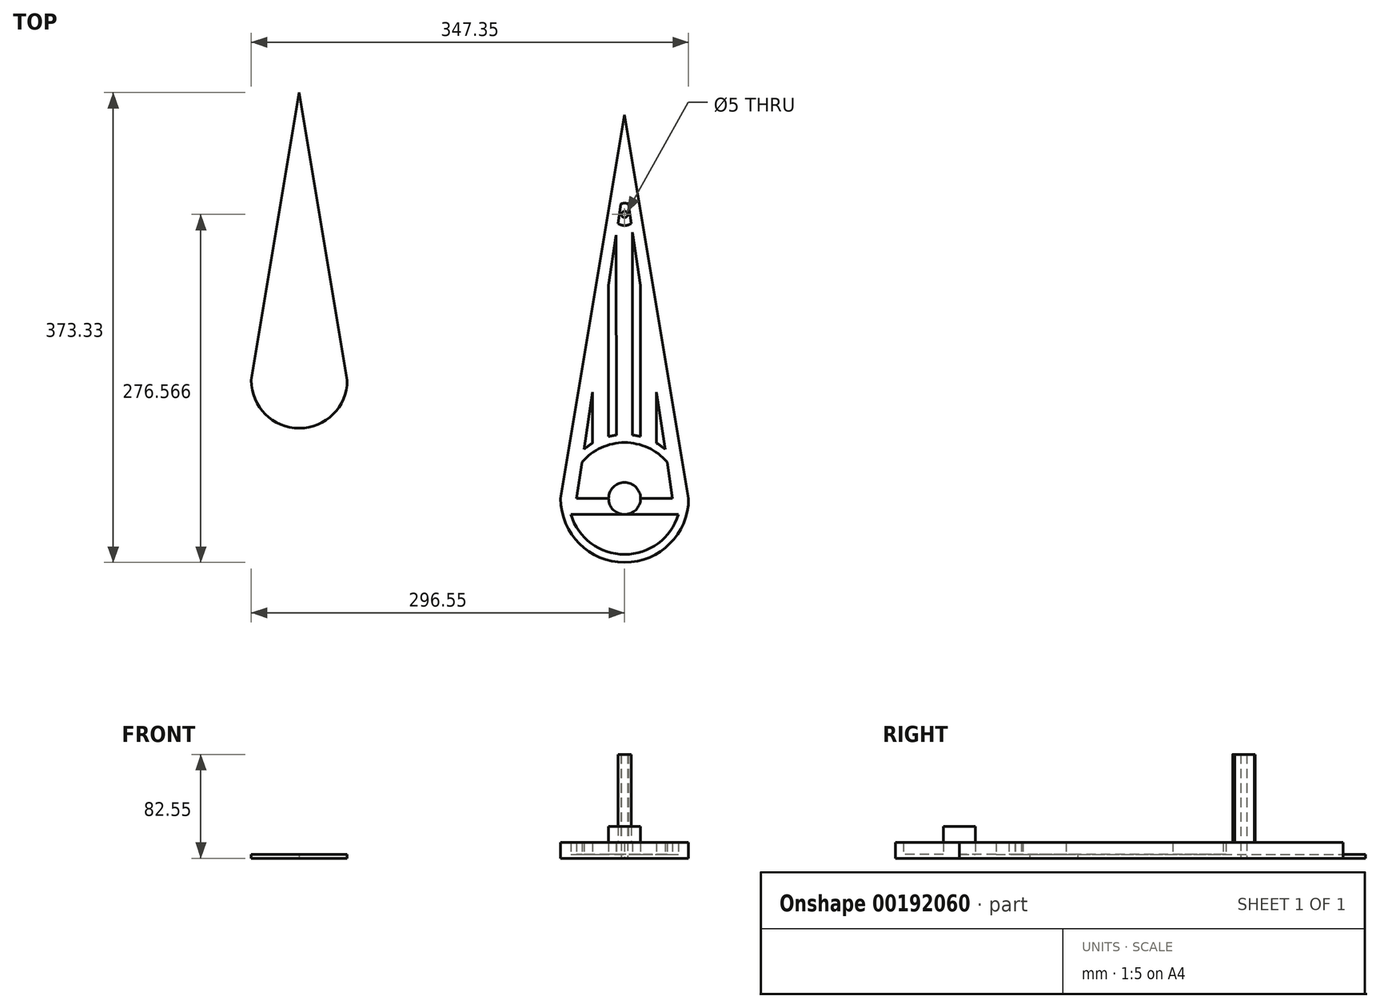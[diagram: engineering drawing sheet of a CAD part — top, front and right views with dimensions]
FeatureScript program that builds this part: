
annotation { "Feature Type Name" : "Feature", "Feature Type Description" : "" }
export const myFeature = defineFeature(function(context is Context, id is Id, definition is map)
    precondition{}
    {
        {
            var Q0;
            Q0=qCreatedBy(makeId("Top.planeOp"),FACE);
            var sketch = newSketch(context, id + "F0", { "sketchPlane" : qUnion([Q0])});
            skLineSegment(sketch, "E0", {"start": v(0, 0) * mm, "end": v(50.8, 0) * mm});
            skLineSegment(sketch, "E1", {"start": v(50.8, 0) * mm, "end": v(101.6, 0) * mm});
            skLineSegment(sketch, "E2", {"start": v(50.8, 0) * mm, "end": v(50.8, 304.8) * mm});
            skLineSegment(sketch, "E3", {"start": v(101.6, 0) * mm, "end": v(50.8, 304.8) * mm});
            skLineSegment(sketch, "E4", {"start": v(0, 0) * mm, "end": v(50.8, 304.8) * mm});
            skCircle(sketch, "E5", {"center": v(50.8, 0) * mm, "radius": 50.8 * mm});
            skLineSegment(sketch, "E6", {"start": v(-258.45, 17.73) * mm, "end": v(-207.65, 17.73) * mm});
            skLineSegment(sketch, "E7", {"start": v(-207.65, 17.73) * mm, "end": v(-156.85, 17.73) * mm});
            skLineSegment(sketch, "E8", {"start": v(-207.65, 17.73) * mm, "end": v(-207.65, 322.53) * mm});
            skLineSegment(sketch, "E9", {"start": v(-156.85, 17.73) * mm, "end": v(-207.65, 322.53) * mm});
            skLineSegment(sketch, "E10", {"start": v(-258.45, 17.73) * mm, "end": v(-207.65, 322.53) * mm});
            skLineSegment(sketch, "E11", {"start": v(-207.65, 93.93) * mm, "end": v(-245.75, 93.93) * mm});
            skLineSegment(sketch, "E12", {"start": v(-207.65, 93.93) * mm, "end": v(-169.55, 93.93) * mm});
            skCircle(sketch, "E13", {"center": v(-207.65, 93.93) * mm, "radius": 38.1 * mm});
            skLineSegment(sketch, "E14", {"start": v(25.4, 0) * mm, "end": v(25.4, 152.4) * mm});
            skLineSegment(sketch, "E15", {"start": v(76.2, 0) * mm, "end": v(76.2, 152.4) * mm});
            skLineSegment(sketch, "E16", {"start": v(38.1, 0) * mm, "end": v(38.1, 228.6) * mm});
            skLineSegment(sketch, "E17", {"start": v(63.5, 0) * mm, "end": v(63.5, 228.6) * mm});
            skLineSegment(sketch, "E18", {"start": v(12.7, 0) * mm, "end": v(12.7, 76.2) * mm});
            skPoint(sketch, "E18.endSnap0", {"position": v(25.4, 76.2) * mm});
            skLineSegment(sketch, "E19", {"start": v(88.9, 0) * mm, "end": v(88.9, 76.2) * mm});
            skLineSegment(sketch, "E20", {"start": v(50.8, 254) * mm, "end": v(12.7, 0) * mm});
            skLineSegment(sketch, "E21", {"start": v(50.8, 254) * mm, "end": v(88.9, 0) * mm});
            skLineSegment(sketch, "E22", {"start": v(57.15, 211.67) * mm, "end": v(57.15, 50.4) * mm});
            skLineSegment(sketch, "E23", {"start": v(44.45, 50.4) * mm, "end": v(44.11, 209.42) * mm});
            skCircle(sketch, "E24", {"center": v(50.8, 0) * mm, "radius": 44.45 * mm});
            skCircle(sketch, "E25", {"center": v(50.8, 0) * mm, "radius": 12.7 * mm});
            skLineSegment(sketch, "E26", {"start": v(8.2, -12.7) * mm, "end": v(93.4, -12.7) * mm});
            skCircle(sketch, "E27", {"center": v(50.8, 225.77) * mm, "radius": 2.5 * mm});
            skCircle(sketch, "E28", {"center": v(50.8, 225.77) * mm, "radius": 8.9 * mm});
            skSolve(sketch);
        }
        {
            var Q0;
            {var subQ0=sQuery(id+"F0.wireOp",EDGE,"E10");var subQ3=sQuery(id+"F0.wireOp",EDGE,"E13");var subQ5=makeQuery(id+"F0.imprint","INTERSECT",VERTEX,{"derivedFrom":[subQ0,subQ3]});Q0=makeQuery(id+"F0.imprint","IMPRINT",FACE,{"disambiguationData":[TD([[makeQuery(id+"F0.imprint","IMPRINT",EDGE,{"disambiguationData":[TD([[subQ5,1.0]])],"derivedFrom":subQ3}),-1.0]])]});}
            var Q1;
            {var subQ0=sQuery(id+"F0.wireOp",EDGE,"E9");var subQ3=sQuery(id+"F0.wireOp",EDGE,"E13");var subQ5=makeQuery(id+"F0.imprint","INTERSECT",VERTEX,{"derivedFrom":[subQ0,subQ3]});Q1=makeQuery(id+"F0.imprint","IMPRINT",FACE,{"disambiguationData":[TD([[makeQuery(id+"F0.imprint","IMPRINT",EDGE,{"disambiguationData":[TD([[subQ5,-1.0]])],"derivedFrom":subQ3}),-1.0]])]});}
            var Q2;
            {var subQ0=sQuery(id+"F0.wireOp",EDGE,"E12");Q2=makeQuery(id+"F0.imprint","IMPRINT",FACE,{"disambiguationData":[TD([[makeQuery(id+"F0.imprint","IMPRINT",EDGE,{"derivedFrom":subQ0}),1.0]])]});}
            var Q3;
            {var subQ0=sQuery(id+"F0.wireOp",EDGE,"E11");Q3=makeQuery(id+"F0.imprint","IMPRINT",FACE,{"disambiguationData":[TD([[makeQuery(id+"F0.imprint","IMPRINT",EDGE,{"derivedFrom":subQ0}),-1.0]])]});}
            var Q4;
            {var subQ0=sQuery(id+"F0.wireOp",EDGE,"E11");Q4=makeQuery(id+"F0.imprint","IMPRINT",FACE,{"disambiguationData":[TD([[makeQuery(id+"F0.imprint","IMPRINT",EDGE,{"derivedFrom":subQ0}),1.0]])]});}
            var Q5;
            {var subQ0=sQuery(id+"F0.wireOp",EDGE,"E12");Q5=makeQuery(id+"F0.imprint","IMPRINT",FACE,{"disambiguationData":[TD([[makeQuery(id+"F0.imprint","IMPRINT",EDGE,{"derivedFrom":subQ0}),-1.0]])]});}
            extrude(context, id + "F1", {"entities" : qUnion([Q0, Q1, Q2, Q3, Q4, Q5]), "depth" : 3.17 * mm});
        }
        {
            var Q0;
            {var subQ1=sQuery(id+"F0.wireOp",EDGE,"E1");var subQ3=sQuery(id+"F0.wireOp",EDGE,"E24");var subQ4=makeQuery(id+"F0.imprint","INTERSECT",VERTEX,{"derivedFrom":[subQ1,subQ3]});Q0=makeQuery(id+"F0.imprint","IMPRINT",FACE,{"disambiguationData":[TD([[makeQuery(id+"F0.imprint","IMPRINT",EDGE,{"disambiguationData":[TD([[subQ4,-1.0]])],"derivedFrom":subQ3}),1.0]])]});}
            var Q1;
            {var subQ0=sQuery(id+"F0.wireOp",EDGE,"E19");var subQ1=sQuery(id+"F0.wireOp",EDGE,"E3");var subQ2=makeQuery(id+"F0.imprint","INTERSECT",VERTEX,{"derivedFrom":[subQ1,subQ0]});Q1=makeQuery(id+"F0.imprint","IMPRINT",FACE,{"disambiguationData":[TD([[makeQuery(id+"F0.imprint","IMPRINT",EDGE,{"disambiguationData":[TD([[subQ2,1.0]])],"derivedFrom":subQ1}),1.0]])]});}
            var Q2;
            {var subQ0=sQuery(id+"F0.wireOp",EDGE,"E18");var subQ1=sQuery(id+"F0.wireOp",EDGE,"E4");var subQ2=makeQuery(id+"F0.imprint","INTERSECT",VERTEX,{"derivedFrom":[subQ1,subQ0]});Q2=makeQuery(id+"F0.imprint","IMPRINT",FACE,{"disambiguationData":[TD([[makeQuery(id+"F0.imprint","IMPRINT",EDGE,{"disambiguationData":[TD([[subQ2,1.0]])],"derivedFrom":subQ1}),-1.0]])]});}
            var Q3;
            {var subQ1=sQuery(id+"F0.wireOp",EDGE,"E0");var subQ3=sQuery(id+"F0.wireOp",EDGE,"E24");var subQ4=makeQuery(id+"F0.imprint","INTERSECT",VERTEX,{"derivedFrom":[subQ1,subQ3]});Q3=makeQuery(id+"F0.imprint","IMPRINT",FACE,{"disambiguationData":[TD([[makeQuery(id+"F0.imprint","IMPRINT",EDGE,{"disambiguationData":[TD([[subQ4,1.0]])],"derivedFrom":subQ3}),1.0]])]});}
            var Q4;
            {var subQ1=sQuery(id+"F0.wireOp",EDGE,"E4");var subQ5=sQuery(id+"F0.wireOp",EDGE,"E14");var subQ6=makeQuery(id+"F0.imprint","INTERSECT",VERTEX,{"derivedFrom":[subQ1,subQ5]});Q4=makeQuery(id+"F0.imprint","IMPRINT",FACE,{"disambiguationData":[TD([[makeQuery(id+"F0.imprint","IMPRINT",EDGE,{"disambiguationData":[TD([[subQ6,1.0]])],"derivedFrom":subQ1}),-1.0]])]});}
            var Q5;
            {var subQ0=sQuery(id+"F0.wireOp",EDGE,"E14");var subQ1=sQuery(id+"F0.wireOp",EDGE,"E4");var subQ2=makeQuery(id+"F0.imprint","INTERSECT",VERTEX,{"derivedFrom":[subQ1,subQ0]});Q5=makeQuery(id+"F0.imprint","IMPRINT",FACE,{"disambiguationData":[TD([[makeQuery(id+"F0.imprint","IMPRINT",EDGE,{"disambiguationData":[TD([[subQ2,-1.0]])],"derivedFrom":subQ1}),-1.0]])]});}
            var Q6;
            {var subQ4=sQuery(id+"F0.wireOp",EDGE,"E16");var subQ6=sQuery(id+"F0.wireOp",EDGE,"E4");var subQ7=makeQuery(id+"F0.imprint","INTERSECT",VERTEX,{"derivedFrom":[subQ6,subQ4]});Q6=makeQuery(id+"F0.imprint","IMPRINT",FACE,{"disambiguationData":[TD([[makeQuery(id+"F0.imprint","IMPRINT",EDGE,{"disambiguationData":[TD([[subQ7,1.0]])],"derivedFrom":subQ4}),-1.0]])]});}
            var Q7;
            {var subQ0=sQuery(id+"F0.wireOp",EDGE,"E3");var subQ3=sQuery(id+"F0.wireOp",EDGE,"E17");var subQ4=makeQuery(id+"F0.imprint","INTERSECT",VERTEX,{"derivedFrom":[subQ0,subQ3]});Q7=makeQuery(id+"F0.imprint","IMPRINT",FACE,{"disambiguationData":[TD([[makeQuery(id+"F0.imprint","IMPRINT",EDGE,{"disambiguationData":[TD([[subQ4,1.0]])],"derivedFrom":subQ3}),1.0]])]});}
            var Q8;
            {var subQ0=sQuery(id+"F0.wireOp",EDGE,"E15");var subQ1=sQuery(id+"F0.wireOp",EDGE,"E3");var subQ2=makeQuery(id+"F0.imprint","INTERSECT",VERTEX,{"derivedFrom":[subQ1,subQ0]});Q8=makeQuery(id+"F0.imprint","IMPRINT",FACE,{"disambiguationData":[TD([[makeQuery(id+"F0.imprint","IMPRINT",EDGE,{"disambiguationData":[TD([[subQ2,-1.0]])],"derivedFrom":subQ1}),1.0]])]});}
            var Q9;
            {var subQ1=sQuery(id+"F0.wireOp",EDGE,"E3");var subQ5=sQuery(id+"F0.wireOp",EDGE,"E15");var subQ6=makeQuery(id+"F0.imprint","INTERSECT",VERTEX,{"derivedFrom":[subQ1,subQ5]});Q9=makeQuery(id+"F0.imprint","IMPRINT",FACE,{"disambiguationData":[TD([[makeQuery(id+"F0.imprint","IMPRINT",EDGE,{"disambiguationData":[TD([[subQ6,1.0]])],"derivedFrom":subQ1}),1.0]])]});}
            var Q10;
            {var subQ0=sQuery(id+"F0.wireOp",EDGE,"E19");var subQ1=sQuery(id+"F0.wireOp",EDGE,"E5");var subQ2=makeQuery(id+"F0.imprint","INTERSECT",VERTEX,{"derivedFrom":[subQ1,subQ0]});Q10=makeQuery(id+"F0.imprint","IMPRINT",FACE,{"disambiguationData":[TD([[makeQuery(id+"F0.imprint","IMPRINT",EDGE,{"disambiguationData":[TD([[subQ2,-1.0]])],"derivedFrom":subQ1}),1.0]])]});}
            var Q11;
            {var subQ0=sQuery(id+"F0.wireOp",EDGE,"E20");var subQ1=sQuery(id+"F0.wireOp",EDGE,"E5");var subQ2=makeQuery(id+"F0.imprint","INTERSECT",VERTEX,{"derivedFrom":[subQ1,subQ0]});Q11=makeQuery(id+"F0.imprint","IMPRINT",FACE,{"disambiguationData":[TD([[makeQuery(id+"F0.imprint","IMPRINT",EDGE,{"disambiguationData":[TD([[subQ2,-1.0]])],"derivedFrom":subQ1}),1.0]])]});}
            var Q12;
            {var subQ0=sQuery(id+"F0.wireOp",EDGE,"E15");var subQ1=sQuery(id+"F0.wireOp",EDGE,"E5");var subQ2=makeQuery(id+"F0.imprint","INTERSECT",VERTEX,{"derivedFrom":[subQ1,subQ0]});Q12=makeQuery(id+"F0.imprint","IMPRINT",FACE,{"disambiguationData":[TD([[makeQuery(id+"F0.imprint","IMPRINT",EDGE,{"disambiguationData":[TD([[subQ2,-1.0]])],"derivedFrom":subQ1}),-1.0]])]});}
            var Q13;
            {var subQ0=sQuery(id+"F0.wireOp",EDGE,"E16");var subQ1=sQuery(id+"F0.wireOp",EDGE,"E5");var subQ2=makeQuery(id+"F0.imprint","INTERSECT",VERTEX,{"derivedFrom":[subQ1,subQ0]});Q13=makeQuery(id+"F0.imprint","IMPRINT",FACE,{"disambiguationData":[TD([[makeQuery(id+"F0.imprint","IMPRINT",EDGE,{"disambiguationData":[TD([[subQ2,-1.0]])],"derivedFrom":subQ1}),-1.0]])]});}
            var Q14;
            {var subQ5=sQuery(id+"F0.wireOp",EDGE,"E22");Q14=makeQuery(id+"F0.imprint","IMPRINT",FACE,{"disambiguationData":[TD([[makeQuery(id+"F0.imprint","IMPRINT",EDGE,{"derivedFrom":subQ5}),-1.0]])]});}
            var Q15;
            {var subQ5=sQuery(id+"F0.wireOp",EDGE,"E23");Q15=makeQuery(id+"F0.imprint","IMPRINT",FACE,{"disambiguationData":[TD([[makeQuery(id+"F0.imprint","IMPRINT",EDGE,{"derivedFrom":subQ5}),-1.0]])]});}
            var Q16;
            {var subQ2=sQuery(id+"F0.wireOp",EDGE,"E2");var subQ4=sQuery(id+"F0.wireOp",EDGE,"E24");var subQ5=makeQuery(id+"F0.imprint","INTERSECT",VERTEX,{"derivedFrom":[subQ2,subQ4]});Q16=makeQuery(id+"F0.imprint","IMPRINT",FACE,{"disambiguationData":[TD([[makeQuery(id+"F0.imprint","IMPRINT",EDGE,{"disambiguationData":[TD([[subQ5,-1.0]])],"derivedFrom":subQ2}),-1.0]])]});}
            var Q17;
            {var subQ3=sQuery(id+"F0.wireOp",EDGE,"E24");var subQ6=sQuery(id+"F0.wireOp",EDGE,"E2");var subQ8=makeQuery(id+"F0.imprint","INTERSECT",VERTEX,{"derivedFrom":[subQ6,subQ3]});Q17=makeQuery(id+"F0.imprint","IMPRINT",FACE,{"disambiguationData":[TD([[makeQuery(id+"F0.imprint","IMPRINT",EDGE,{"disambiguationData":[TD([[subQ8,-1.0]])],"derivedFrom":subQ6}),1.0]])]});}
            var Q18;
            {var subQ0=sQuery(id+"F0.wireOp",EDGE,"E16");var subQ1=sQuery(id+"F0.wireOp",EDGE,"E5");var subQ2=makeQuery(id+"F0.imprint","INTERSECT",VERTEX,{"derivedFrom":[subQ1,subQ0]});Q18=makeQuery(id+"F0.imprint","IMPRINT",FACE,{"disambiguationData":[TD([[makeQuery(id+"F0.imprint","IMPRINT",EDGE,{"disambiguationData":[TD([[subQ2,-1.0]])],"derivedFrom":subQ1}),1.0]])]});}
            var Q19;
            {var subQ0=sQuery(id+"F0.wireOp",EDGE,"E14");var subQ1=sQuery(id+"F0.wireOp",EDGE,"E5");var subQ2=makeQuery(id+"F0.imprint","INTERSECT",VERTEX,{"derivedFrom":[subQ1,subQ0]});Q19=makeQuery(id+"F0.imprint","IMPRINT",FACE,{"disambiguationData":[TD([[makeQuery(id+"F0.imprint","IMPRINT",EDGE,{"disambiguationData":[TD([[subQ2,-1.0]])],"derivedFrom":subQ1}),1.0]])]});}
            var Q20;
            {var subQ0=sQuery(id+"F0.wireOp",EDGE,"E15");var subQ1=sQuery(id+"F0.wireOp",EDGE,"E5");var subQ2=makeQuery(id+"F0.imprint","INTERSECT",VERTEX,{"derivedFrom":[subQ1,subQ0]});Q20=makeQuery(id+"F0.imprint","IMPRINT",FACE,{"disambiguationData":[TD([[makeQuery(id+"F0.imprint","IMPRINT",EDGE,{"disambiguationData":[TD([[subQ2,-1.0]])],"derivedFrom":subQ1}),1.0]])]});}
            var Q21;
            {var subQ0=sQuery(id+"F0.wireOp",EDGE,"E21");var subQ1=sQuery(id+"F0.wireOp",EDGE,"E5");var subQ2=makeQuery(id+"F0.imprint","INTERSECT",VERTEX,{"derivedFrom":[subQ1,subQ0]});Q21=makeQuery(id+"F0.imprint","IMPRINT",FACE,{"disambiguationData":[TD([[makeQuery(id+"F0.imprint","IMPRINT",EDGE,{"disambiguationData":[TD([[subQ2,-1.0]])],"derivedFrom":subQ1}),1.0]])]});}
            var Q22;
            {var subQ1=sQuery(id+"F0.wireOp",EDGE,"E5");var subQ5=sQuery(id+"F0.wireOp",EDGE,"E3");var subQ8=makeQuery(id+"F0.imprint","INTERSECT",VERTEX,{"derivedFrom":[subQ5,subQ1]});Q22=makeQuery(id+"F0.imprint","IMPRINT",FACE,{"disambiguationData":[TD([[makeQuery(id+"F0.imprint","IMPRINT",EDGE,{"disambiguationData":[TD([[subQ8,-1.0]])],"derivedFrom":subQ1}),1.0]])]});}
            var Q23;
            {var subQ0=sQuery(id+"F0.wireOp",EDGE,"E26");var subQ1=sQuery(id+"F0.wireOp",EDGE,"E24");var subQ2=makeQuery(id+"F0.imprint","INTERSECT",VERTEX,{"disambiguationData":[OD(0.0)],"derivedFrom":[subQ1,subQ0]});Q23=makeQuery(id+"F0.imprint","IMPRINT",FACE,{"disambiguationData":[TD([[makeQuery(id+"F0.imprint","IMPRINT",EDGE,{"disambiguationData":[TD([[subQ2,1.0]])],"derivedFrom":subQ1}),-1.0]])]});}
            var Q24;
            {var subQ1=sQuery(id+"F0.wireOp",EDGE,"E5");var subQ5=sQuery(id+"F0.wireOp",EDGE,"E4");var subQ6=makeQuery(id+"F0.imprint","INTERSECT",VERTEX,{"derivedFrom":[subQ5,subQ1]});Q24=makeQuery(id+"F0.imprint","IMPRINT",FACE,{"disambiguationData":[TD([[makeQuery(id+"F0.imprint","IMPRINT",EDGE,{"disambiguationData":[TD([[subQ6,1.0]])],"derivedFrom":subQ1}),1.0]])]});}
            var Q25;
            {var subQ1=sQuery(id+"F0.wireOp",EDGE,"E19");var subQ3=sQuery(id+"F0.wireOp",EDGE,"E24");var subQ4=makeQuery(id+"F0.imprint","INTERSECT",VERTEX,{"derivedFrom":[subQ1,subQ3]});Q25=makeQuery(id+"F0.imprint","IMPRINT",FACE,{"disambiguationData":[TD([[makeQuery(id+"F0.imprint","IMPRINT",EDGE,{"disambiguationData":[TD([[subQ4,-1.0]])],"derivedFrom":subQ3}),1.0]])]});}
            var Q26;
            {var subQ1=sQuery(id+"F0.wireOp",EDGE,"E18");var subQ3=sQuery(id+"F0.wireOp",EDGE,"E24");var subQ4=makeQuery(id+"F0.imprint","INTERSECT",VERTEX,{"derivedFrom":[subQ1,subQ3]});Q26=makeQuery(id+"F0.imprint","IMPRINT",FACE,{"disambiguationData":[TD([[makeQuery(id+"F0.imprint","IMPRINT",EDGE,{"disambiguationData":[TD([[subQ4,1.0]])],"derivedFrom":subQ3}),1.0]])]});}
            var Q27;
            {var subQ0=sQuery(id+"F0.wireOp",EDGE,"E26");var subQ1=sQuery(id+"F0.wireOp",EDGE,"E24");var subQ2=makeQuery(id+"F0.imprint","INTERSECT",VERTEX,{"disambiguationData":[OD(1.0)],"derivedFrom":[subQ1,subQ0]});Q27=makeQuery(id+"F0.imprint","IMPRINT",FACE,{"disambiguationData":[TD([[makeQuery(id+"F0.imprint","IMPRINT",EDGE,{"disambiguationData":[TD([[subQ2,-1.0]])],"derivedFrom":subQ1}),1.0]])]});}
            var Q28;
            {var subQ0=sQuery(id+"F0.wireOp",EDGE,"E26");var subQ1=sQuery(id+"F0.wireOp",EDGE,"E24");var subQ2=makeQuery(id+"F0.imprint","INTERSECT",VERTEX,{"disambiguationData":[OD(0.0)],"derivedFrom":[subQ1,subQ0]});Q28=makeQuery(id+"F0.imprint","IMPRINT",FACE,{"disambiguationData":[TD([[makeQuery(id+"F0.imprint","IMPRINT",EDGE,{"disambiguationData":[TD([[subQ2,1.0]])],"derivedFrom":subQ1}),1.0]])]});}
            var Q29;
            {var subQ3=sQuery(id+"F0.wireOp",EDGE,"E25");var subQ6=makeQuery(id+"F0.imprint","INTERSECT",VERTEX,{"derivedFrom":[subQ3,sQuery(id+"F0.wireOp",EDGE,"E26")]});Q29=makeQuery(id+"F0.imprint","IMPRINT",FACE,{"disambiguationData":[TD([[makeQuery(id+"F0.imprint","IMPRINT",EDGE,{"disambiguationData":[TD([[subQ6,1.0]])],"derivedFrom":subQ3}),1.0]])]});}
            var Q30;
            {var subQ0=sQuery(id+"F0.wireOp",EDGE,"E2");var subQ3=sQuery(id+"F0.wireOp",EDGE,"E25");var subQ5=makeQuery(id+"F0.imprint","INTERSECT",VERTEX,{"derivedFrom":[subQ0,subQ3]});Q30=makeQuery(id+"F0.imprint","IMPRINT",FACE,{"disambiguationData":[TD([[makeQuery(id+"F0.imprint","IMPRINT",EDGE,{"disambiguationData":[TD([[subQ5,1.0]])],"derivedFrom":subQ0}),-1.0]])]});}
            var Q31;
            {var subQ0=sQuery(id+"F0.wireOp",EDGE,"E2");var subQ3=sQuery(id+"F0.wireOp",EDGE,"E25");var subQ5=makeQuery(id+"F0.imprint","INTERSECT",VERTEX,{"derivedFrom":[subQ0,subQ3]});Q31=makeQuery(id+"F0.imprint","IMPRINT",FACE,{"disambiguationData":[TD([[makeQuery(id+"F0.imprint","IMPRINT",EDGE,{"disambiguationData":[TD([[subQ5,1.0]])],"derivedFrom":subQ0}),1.0]])]});}
            var Q32;
            {var subQ0=sQuery(id+"F0.wireOp",EDGE,"E28");var subQ1=sQuery(id+"F0.wireOp",EDGE,"E21");var subQ2=makeQuery(id+"F0.imprint","INTERSECT",VERTEX,{"disambiguationData":[OD(0.0)],"derivedFrom":[subQ1,subQ0]});Q32=makeQuery(id+"F0.imprint","IMPRINT",FACE,{"disambiguationData":[TD([[makeQuery(id+"F0.imprint","IMPRINT",EDGE,{"disambiguationData":[TD([[subQ2,-1.0]])],"derivedFrom":subQ1}),1.0]])]});}
            var Q33;
            {var subQ0=sQuery(id+"F0.wireOp",EDGE,"E28");var subQ1=sQuery(id+"F0.wireOp",EDGE,"E20");var subQ2=makeQuery(id+"F0.imprint","INTERSECT",VERTEX,{"disambiguationData":[OD(0.0)],"derivedFrom":[subQ1,subQ0]});Q33=makeQuery(id+"F0.imprint","IMPRINT",FACE,{"disambiguationData":[TD([[makeQuery(id+"F0.imprint","IMPRINT",EDGE,{"disambiguationData":[TD([[subQ2,-1.0]])],"derivedFrom":subQ1}),-1.0]])]});}
            var Q34;
            {var subQ1=sQuery(id+"F0.wireOp",EDGE,"E2");var subQ4=sQuery(id+"F0.wireOp",EDGE,"E28");var subQ9=makeQuery(id+"F0.imprint","INTERSECT",VERTEX,{"disambiguationData":[OD(0.0)],"derivedFrom":[subQ1,subQ4]});Q34=makeQuery(id+"F0.imprint","IMPRINT",FACE,{"disambiguationData":[TD([[makeQuery(id+"F0.imprint","IMPRINT",EDGE,{"disambiguationData":[TD([[subQ9,-1.0]])],"derivedFrom":subQ1}),1.0]])]});}
            var Q35;
            {var subQ1=sQuery(id+"F0.wireOp",EDGE,"E2");var subQ4=sQuery(id+"F0.wireOp",EDGE,"E28");var subQ9=makeQuery(id+"F0.imprint","INTERSECT",VERTEX,{"disambiguationData":[OD(0.0)],"derivedFrom":[subQ1,subQ4]});Q35=makeQuery(id+"F0.imprint","IMPRINT",FACE,{"disambiguationData":[TD([[makeQuery(id+"F0.imprint","IMPRINT",EDGE,{"disambiguationData":[TD([[subQ9,-1.0]])],"derivedFrom":subQ1}),-1.0]])]});}
            var Q36;
            {var subQ1=sQuery(id+"F0.wireOp",EDGE,"E2");var subQ3=sQuery(id+"F0.wireOp",EDGE,"E28");var subQ4=makeQuery(id+"F0.imprint","INTERSECT",VERTEX,{"disambiguationData":[OD(1.0)],"derivedFrom":[subQ1,subQ3]});Q36=makeQuery(id+"F0.imprint","IMPRINT",FACE,{"disambiguationData":[TD([[makeQuery(id+"F0.imprint","IMPRINT",EDGE,{"disambiguationData":[TD([[subQ4,1.0]])],"derivedFrom":subQ3}),-1.0]])]});}
            var Q37;
            {var subQ1=sQuery(id+"F0.wireOp",EDGE,"E2");var subQ3=sQuery(id+"F0.wireOp",EDGE,"E28");var subQ4=makeQuery(id+"F0.imprint","INTERSECT",VERTEX,{"disambiguationData":[OD(1.0)],"derivedFrom":[subQ1,subQ3]});Q37=makeQuery(id+"F0.imprint","IMPRINT",FACE,{"disambiguationData":[TD([[makeQuery(id+"F0.imprint","IMPRINT",EDGE,{"disambiguationData":[TD([[subQ4,-1.0]])],"derivedFrom":subQ3}),-1.0]])]});}
            extrude(context, id + "F2", {"entities" : qUnion([Q0, Q1, Q2, Q3, Q4, Q5, Q6, Q7, Q8, Q9, Q10, Q11, Q12, Q13, Q14, Q15, Q16, Q17, Q18, Q19, Q20, Q21, Q22, Q23, Q24, Q25, Q26, Q27, Q28, Q29, Q30, Q31, Q32, Q33, Q34, Q35, Q36, Q37]), "depth" : 12.7 * mm});
        }
        {
            var Q0;
            {var subQ0=sQuery(id+"F0.wireOp",EDGE,"E22");Q0=makeQuery(id+"F0.imprint","IMPRINT",FACE,{"disambiguationData":[TD([[makeQuery(id+"F0.imprint","IMPRINT",EDGE,{"derivedFrom":subQ0}),1.0]])]});}
            var Q1;
            {var subQ0=sQuery(id+"F0.wireOp",EDGE,"E23");Q1=makeQuery(id+"F0.imprint","IMPRINT",FACE,{"disambiguationData":[TD([[makeQuery(id+"F0.imprint","IMPRINT",EDGE,{"derivedFrom":subQ0}),1.0]])]});}
            var Q2;
            {var subQ0=sQuery(id+"F0.wireOp",EDGE,"E14");var subQ1=sQuery(id+"F0.wireOp",EDGE,"E5");var subQ2=makeQuery(id+"F0.imprint","INTERSECT",VERTEX,{"derivedFrom":[subQ1,subQ0]});Q2=makeQuery(id+"F0.imprint","IMPRINT",FACE,{"disambiguationData":[TD([[makeQuery(id+"F0.imprint","IMPRINT",EDGE,{"disambiguationData":[TD([[subQ2,-1.0]])],"derivedFrom":subQ1}),-1.0]])]});}
            var Q3;
            {var subQ0=sQuery(id+"F0.wireOp",EDGE,"E21");var subQ1=sQuery(id+"F0.wireOp",EDGE,"E5");var subQ2=makeQuery(id+"F0.imprint","INTERSECT",VERTEX,{"derivedFrom":[subQ1,subQ0]});Q3=makeQuery(id+"F0.imprint","IMPRINT",FACE,{"disambiguationData":[TD([[makeQuery(id+"F0.imprint","IMPRINT",EDGE,{"disambiguationData":[TD([[subQ2,-1.0]])],"derivedFrom":subQ1}),-1.0]])]});}
            var Q4;
            {var subQ4=sQuery(id+"F0.wireOp",EDGE,"E0");var subQ8=sQuery(id+"F0.wireOp",EDGE,"E24");var subQ9=makeQuery(id+"F0.imprint","INTERSECT",VERTEX,{"derivedFrom":[subQ4,subQ8]});Q4=makeQuery(id+"F0.imprint","IMPRINT",FACE,{"disambiguationData":[TD([[makeQuery(id+"F0.imprint","IMPRINT",EDGE,{"disambiguationData":[TD([[subQ9,-1.0]])],"derivedFrom":subQ8}),1.0]])]});}
            var Q5;
            {var subQ0=sQuery(id+"F0.wireOp",EDGE,"E15");var subQ1=sQuery(id+"F0.wireOp",EDGE,"E1");var subQ2=makeQuery(id+"F0.imprint","INTERSECT",VERTEX,{"derivedFrom":[subQ1,subQ0]});Q5=makeQuery(id+"F0.imprint","IMPRINT",FACE,{"disambiguationData":[TD([[makeQuery(id+"F0.imprint","IMPRINT",EDGE,{"disambiguationData":[TD([[subQ2,-1.0]])],"derivedFrom":subQ0}),1.0]])]});}
            var Q6;
            {var subQ0=sQuery(id+"F0.wireOp",EDGE,"E15");var subQ1=sQuery(id+"F0.wireOp",EDGE,"E1");var subQ2=makeQuery(id+"F0.imprint","INTERSECT",VERTEX,{"derivedFrom":[subQ1,subQ0]});Q6=makeQuery(id+"F0.imprint","IMPRINT",FACE,{"disambiguationData":[TD([[makeQuery(id+"F0.imprint","IMPRINT",EDGE,{"disambiguationData":[TD([[subQ2,-1.0]])],"derivedFrom":subQ0}),-1.0]])]});}
            var Q7;
            {var subQ0=sQuery(id+"F0.wireOp",EDGE,"E14");var subQ1=sQuery(id+"F0.wireOp",EDGE,"E0");var subQ2=makeQuery(id+"F0.imprint","INTERSECT",VERTEX,{"derivedFrom":[subQ1,subQ0]});Q7=makeQuery(id+"F0.imprint","IMPRINT",FACE,{"disambiguationData":[TD([[makeQuery(id+"F0.imprint","IMPRINT",EDGE,{"disambiguationData":[TD([[subQ2,-1.0]])],"derivedFrom":subQ0}),1.0]])]});}
            var Q8;
            {var subQ0=sQuery(id+"F0.wireOp",EDGE,"E14");var subQ1=sQuery(id+"F0.wireOp",EDGE,"E0");var subQ2=makeQuery(id+"F0.imprint","INTERSECT",VERTEX,{"derivedFrom":[subQ1,subQ0]});Q8=makeQuery(id+"F0.imprint","IMPRINT",FACE,{"disambiguationData":[TD([[makeQuery(id+"F0.imprint","IMPRINT",EDGE,{"disambiguationData":[TD([[subQ2,-1.0]])],"derivedFrom":subQ0}),-1.0]])]});}
            var Q9;
            {var subQ0=sQuery(id+"F0.wireOp",EDGE,"E25");var subQ1=sQuery(id+"F0.wireOp",EDGE,"E2");var subQ2=makeQuery(id+"F0.imprint","INTERSECT",VERTEX,{"derivedFrom":[subQ1,subQ0]});Q9=makeQuery(id+"F0.imprint","IMPRINT",FACE,{"disambiguationData":[TD([[makeQuery(id+"F0.imprint","IMPRINT",EDGE,{"disambiguationData":[TD([[subQ2,-1.0]])],"derivedFrom":subQ1}),1.0]])]});}
            var Q10;
            {var subQ0=sQuery(id+"F0.wireOp",EDGE,"E25");var subQ1=sQuery(id+"F0.wireOp",EDGE,"E2");var subQ2=makeQuery(id+"F0.imprint","INTERSECT",VERTEX,{"derivedFrom":[subQ1,subQ0]});Q10=makeQuery(id+"F0.imprint","IMPRINT",FACE,{"disambiguationData":[TD([[makeQuery(id+"F0.imprint","IMPRINT",EDGE,{"disambiguationData":[TD([[subQ2,-1.0]])],"derivedFrom":subQ1}),-1.0]])]});}
            var Q11;
            {var subQ0=sQuery(id+"F0.wireOp",EDGE,"E26");var subQ1=sQuery(id+"F0.wireOp",EDGE,"E24");var subQ2=makeQuery(id+"F0.imprint","INTERSECT",VERTEX,{"disambiguationData":[OD(0.0)],"derivedFrom":[subQ1,subQ0]});Q11=makeQuery(id+"F0.imprint","IMPRINT",FACE,{"disambiguationData":[TD([[makeQuery(id+"F0.imprint","IMPRINT",EDGE,{"disambiguationData":[TD([[subQ2,-1.0]])],"derivedFrom":subQ1}),1.0]])]});}
            var Q12;
            {var subQ0=sQuery(id+"F0.wireOp",EDGE,"E28");var subQ1=sQuery(id+"F0.wireOp",EDGE,"E21");var subQ2=makeQuery(id+"F0.imprint","INTERSECT",VERTEX,{"disambiguationData":[OD(0.0)],"derivedFrom":[subQ1,subQ0]});Q12=makeQuery(id+"F0.imprint","IMPRINT",FACE,{"disambiguationData":[TD([[makeQuery(id+"F0.imprint","IMPRINT",EDGE,{"disambiguationData":[TD([[subQ2,-1.0]])],"derivedFrom":subQ1}),1.0]])]});}
            var Q13;
            {var subQ1=sQuery(id+"F0.wireOp",EDGE,"E2");var subQ4=sQuery(id+"F0.wireOp",EDGE,"E28");var subQ9=makeQuery(id+"F0.imprint","INTERSECT",VERTEX,{"disambiguationData":[OD(0.0)],"derivedFrom":[subQ1,subQ4]});Q13=makeQuery(id+"F0.imprint","IMPRINT",FACE,{"disambiguationData":[TD([[makeQuery(id+"F0.imprint","IMPRINT",EDGE,{"disambiguationData":[TD([[subQ9,-1.0]])],"derivedFrom":subQ1}),-1.0]])]});}
            var Q14;
            {var subQ1=sQuery(id+"F0.wireOp",EDGE,"E2");var subQ4=sQuery(id+"F0.wireOp",EDGE,"E28");var subQ9=makeQuery(id+"F0.imprint","INTERSECT",VERTEX,{"disambiguationData":[OD(0.0)],"derivedFrom":[subQ1,subQ4]});Q14=makeQuery(id+"F0.imprint","IMPRINT",FACE,{"disambiguationData":[TD([[makeQuery(id+"F0.imprint","IMPRINT",EDGE,{"disambiguationData":[TD([[subQ9,-1.0]])],"derivedFrom":subQ1}),1.0]])]});}
            var Q15;
            {var subQ0=sQuery(id+"F0.wireOp",EDGE,"E28");var subQ1=sQuery(id+"F0.wireOp",EDGE,"E20");var subQ2=makeQuery(id+"F0.imprint","INTERSECT",VERTEX,{"disambiguationData":[OD(0.0)],"derivedFrom":[subQ1,subQ0]});Q15=makeQuery(id+"F0.imprint","IMPRINT",FACE,{"disambiguationData":[TD([[makeQuery(id+"F0.imprint","IMPRINT",EDGE,{"disambiguationData":[TD([[subQ2,-1.0]])],"derivedFrom":subQ1}),-1.0]])]});}
            var Q16;
            {var subQ1=sQuery(id+"F0.wireOp",EDGE,"E2");var subQ3=sQuery(id+"F0.wireOp",EDGE,"E28");var subQ4=makeQuery(id+"F0.imprint","INTERSECT",VERTEX,{"disambiguationData":[OD(1.0)],"derivedFrom":[subQ1,subQ3]});Q16=makeQuery(id+"F0.imprint","IMPRINT",FACE,{"disambiguationData":[TD([[makeQuery(id+"F0.imprint","IMPRINT",EDGE,{"disambiguationData":[TD([[subQ4,1.0]])],"derivedFrom":subQ3}),-1.0]])]});}
            var Q17;
            {var subQ1=sQuery(id+"F0.wireOp",EDGE,"E2");var subQ3=sQuery(id+"F0.wireOp",EDGE,"E28");var subQ4=makeQuery(id+"F0.imprint","INTERSECT",VERTEX,{"disambiguationData":[OD(1.0)],"derivedFrom":[subQ1,subQ3]});Q17=makeQuery(id+"F0.imprint","IMPRINT",FACE,{"disambiguationData":[TD([[makeQuery(id+"F0.imprint","IMPRINT",EDGE,{"disambiguationData":[TD([[subQ4,-1.0]])],"derivedFrom":subQ3}),-1.0]])]});}
            extrude(context, id + "F3", {"entities" : qUnion([Q0, Q1, Q2, Q3, Q4, Q5, Q6, Q7, Q8, Q9, Q10, Q11, Q12, Q13, Q14, Q15, Q16, Q17]), "operationType" : NewBodyOperationType.ADD, "depth" : 3.17 * mm});
        }
        {
            var Q0;
            Q0=makeQuery(id+"F2.opExtrude","CAP_FACE",FACE,{"disambiguationData":[OSD([sQuery(id+"F0.wireOp",EDGE,"E0"),sQuery(id+"F0.wireOp",EDGE,"E1"),sQuery(id+"F0.wireOp",EDGE,"E3"),sQuery(id+"F0.wireOp",EDGE,"E4"),sQuery(id+"F0.wireOp",EDGE,"E5"),sQuery(id+"F0.wireOp",EDGE,"E14"),sQuery(id+"F0.wireOp",EDGE,"E15"),sQuery(id+"F0.wireOp",EDGE,"E16"),sQuery(id+"F0.wireOp",EDGE,"E17"),sQuery(id+"F0.wireOp",EDGE,"E20"),sQuery(id+"F0.wireOp",EDGE,"E21"),sQuery(id+"F0.wireOp",EDGE,"E22"),sQuery(id+"F0.wireOp",EDGE,"E23"),sQuery(id+"F0.wireOp",EDGE,"E24"),sQuery(id+"F0.wireOp",EDGE,"E25"),sQuery(id+"F0.wireOp",EDGE,"E26")])],"isStart":false});
            var sketch = newSketch(context, id + "F4", { "sketchPlane" : qUnion([Q0])});
            skCircle(sketch, "E29", {"center": v(50.8, 0) * mm, "radius": 12.7 * mm});
            skSolve(sketch);
        }
        {
            var Q0;
            {var subQ0=sQuery(id+"F4.wireOp",EDGE,"E29");var subQ1=makeQuery(id+"F4.imprint","INTERSECT",VERTEX,{"derivedFrom":[makeQuery(id+"F2.opExtrude","CAP_EDGE",EDGE,{"disambiguationData":[OSD([sQuery(id+"F0.wireOp",EDGE,"E0")])],"isStart":false}),subQ0]});Q0=makeQuery(id+"F4.imprint","IMPRINT",FACE,{"disambiguationData":[TD([[makeQuery(id+"F4.imprint","IMPRINT",EDGE,{"disambiguationData":[TD([[subQ1,1.0]])],"derivedFrom":subQ0}),1.0]])]});}
            extrude(context, id + "F5", {"entities" : qUnion([Q0]), "depth" : 12.7 * mm});
        }
        {
            var Q0;
            {var subQ0=sQuery(id+"F0.wireOp",EDGE,"E27");var subQ1=sQuery(id+"F0.wireOp",EDGE,"E2");var subQ2=makeQuery(id+"F0.imprint","INTERSECT",VERTEX,{"disambiguationData":[OD(0.0)],"derivedFrom":[subQ1,subQ0]});Q0=makeQuery(id+"F0.imprint","IMPRINT",FACE,{"disambiguationData":[TD([[makeQuery(id+"F0.imprint","IMPRINT",EDGE,{"disambiguationData":[TD([[subQ2,-1.0]])],"derivedFrom":subQ1}),-1.0]])]});}
            var Q1;
            {var subQ0=sQuery(id+"F0.wireOp",EDGE,"E27");var subQ1=sQuery(id+"F0.wireOp",EDGE,"E2");var subQ2=makeQuery(id+"F0.imprint","INTERSECT",VERTEX,{"disambiguationData":[OD(0.0)],"derivedFrom":[subQ1,subQ0]});Q1=makeQuery(id+"F0.imprint","IMPRINT",FACE,{"disambiguationData":[TD([[makeQuery(id+"F0.imprint","IMPRINT",EDGE,{"disambiguationData":[TD([[subQ2,-1.0]])],"derivedFrom":subQ1}),1.0]])]});}
            extrude(context, id + "F6", {"entities" : qUnion([Q0, Q1]), "operationType" : NewBodyOperationType.ADD, "depth" : 82.55 * mm});
        }
    });
